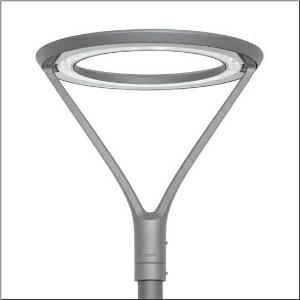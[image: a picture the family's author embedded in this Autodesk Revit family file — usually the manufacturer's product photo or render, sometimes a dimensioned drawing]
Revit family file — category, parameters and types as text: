
# Revit family: dl_r__20_led___pl1_2s_5xa51283ws008_cda1
name_source: partatom
category: Lighting Fixtures
units: mm (PartAtom-declared; Revit-internal decimal feet)

## family parameters
Cut with Voids When Loaded = No
Host = Face
Light Source = No
Part Type = Normal
Room Calculation Point = No
Round Connector Dimension = Use Diameter
Shared = No

## types (1)
- --- (1 x LED 3000K / CRI = 80 (unbekannt), 3040 lm, 3000K)
    Apparent Load = 36 VA
    CIE Flux Codes = 34 78 98 100 100
    Color Rendering = 80
    Color Temperature = 3000K
    Default Elevation = 1800 mm
    Description = DL® 20 LED, mast luminaire, primary light control with reflector, highly specular, primary optical cover: cover, of toughened safety glass of clear glass with excellent transmission level, light distribution: PL1.2s, light emission: direct distribution, primary light characteristic: symmetric, installation type: post-top, LED High Power LED, rated luminous flux: 3.040 lm, light colour: 830, colour temperature: 3000K, control gear: ECG Plus, control: overheat protection, power reduction, digital communication interface, constant luminous flux control, time-dependent luminous flux control, flexible luminous flux parameterisation, electronic power reduction, mains connection: 220..240V, 50/60Hz, connection cable pre-assembled, cable length: 5 m, start of lifetime: 36 W, end of lifetime: 36 W, reduction: 17 W, luminaire housing, upper part, of cast aluminium, powder-coated, Siteco® metallic grey (DB 702S), diameter: 690 mm, height: 690mm, spigot size: 76mm (post-top), luminaire housing, of cast aluminium, powder-coated, Siteco® metallic grey (DB 702S), protection rating (complete): IP66, insulation class (complete): insulation class II (safety insulation), certification: CE, ENEC, VDE, impact resistance: IK08, permissible ambient temperature for indoor applications: -25..+35°C, standard-compliant lighting for roads and squares, packaging unit: 1 piece

Light Distribution: PL1.2s
    Height = 690 mm
    Lamp = 1 x LED 3000K / CRI >= 80 (unbekannt)
    Lamp Light Flux = 3040 lm
    Lamp count = 1
    Length = 690 mm
    Luminous efficacy = 86 lm/W
    Manufacturer = Siteco
    ModVariant = No
    Model = 5XA51283WS008
    Number of Poles = 1
    OnlyDefault = Yes
    Power Factor = 1
    Product Name = DL® 20 LED | PL1.2s
    Product group = mast luminaire | pylon top
    ProductGroupID = 6100
    Protection Class = Protection class II
    Protection Degree = IP 66
    RLX_Detail_Level = 1
    RlxData = <blob elided: 204073 chars, md5=1a7ddbef>
    Socket = socket
    Standby Power = 0 W
    System Light Flux = 3040 lm
    System Power = 36 W
    Type Comments = factory setting: luminous flux: 100 % | dim-lin: 254 | 468 mA
    Type Image = l_1006001.jpg
    URL = http://relux.com
    VarID = @adj_141597
    Voltage = 0 V
    Weight = 0.00 kg
    Width = 0 mm  [stored 0 ft]

note: [stored X ft] marks values corroborated as IEEE doubles in the binary element streams (Revit-internal decimal feet)

## geometry (parser evidence)
native form markers: Blend x4, Sweep x10
no freeform markers — native parametric forms only
